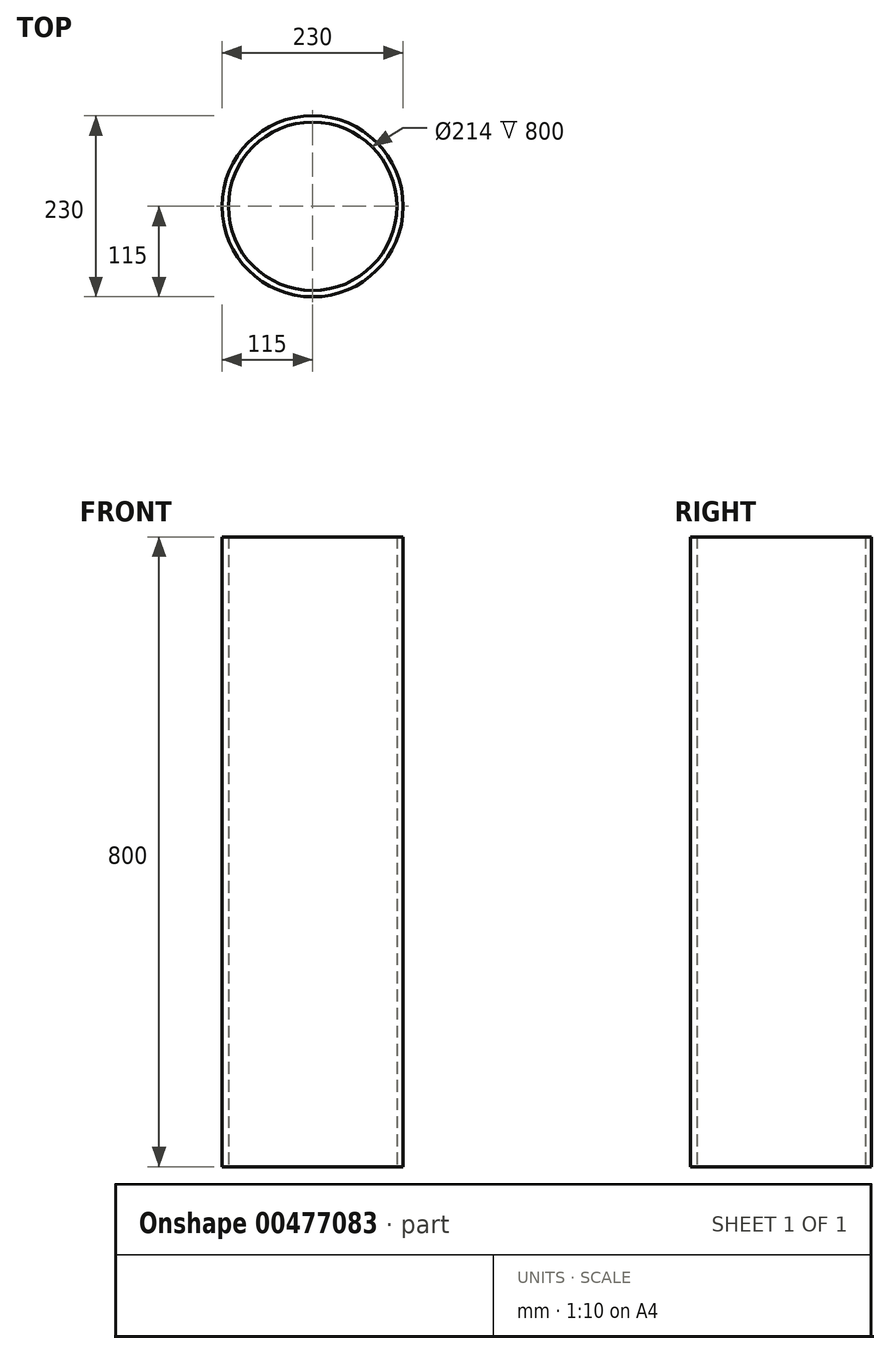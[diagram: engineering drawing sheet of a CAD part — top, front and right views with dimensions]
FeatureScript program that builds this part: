
annotation { "Feature Type Name" : "Feature", "Feature Type Description" : "" }
export const myFeature = defineFeature(function(context is Context, id is Id, definition is map)
    precondition{}
    {
        {
            var Q0;
            Q0=qCreatedBy(makeId("Top.planeOp"),FACE);
            var sketch = newSketch(context, id + "F0", { "sketchPlane" : qUnion([Q0])});
            skCircle(sketch, "E0", {"center": v(0, 0) * mm, "radius": 115 * mm});
            skSolve(sketch);
        }
        {
            var Q0;
            Q0=qCreatedBy(makeId("Top.planeOp"),FACE);
            var sketch = newSketch(context, id + "F1", { "sketchPlane" : qUnion([Q0])});
            skCircle(sketch, "E1", {"center": v(0, 0) * mm, "radius": 107 * mm});
            skSolve(sketch);
        }
        {
            var Q0;
            Q0 = qSketchRegion(id + "F0", true);
            extrude(context, id + "F2", {"entities" : qUnion([Q0]), "depth" : 800 * mm, "offsetDistance" : 25 * mm});
        }
        {
            var Q0;
            Q0 = qSketchRegion(id + "F1", true);
            extrude(context, id + "F3", {"entities" : qUnion([Q0]), "operationType" : NewBodyOperationType.REMOVE, "endBound" : BoundingType.THROUGH_ALL, "depth" : 25 * mm, "offsetDistance" : 25 * mm});
        }
    });
